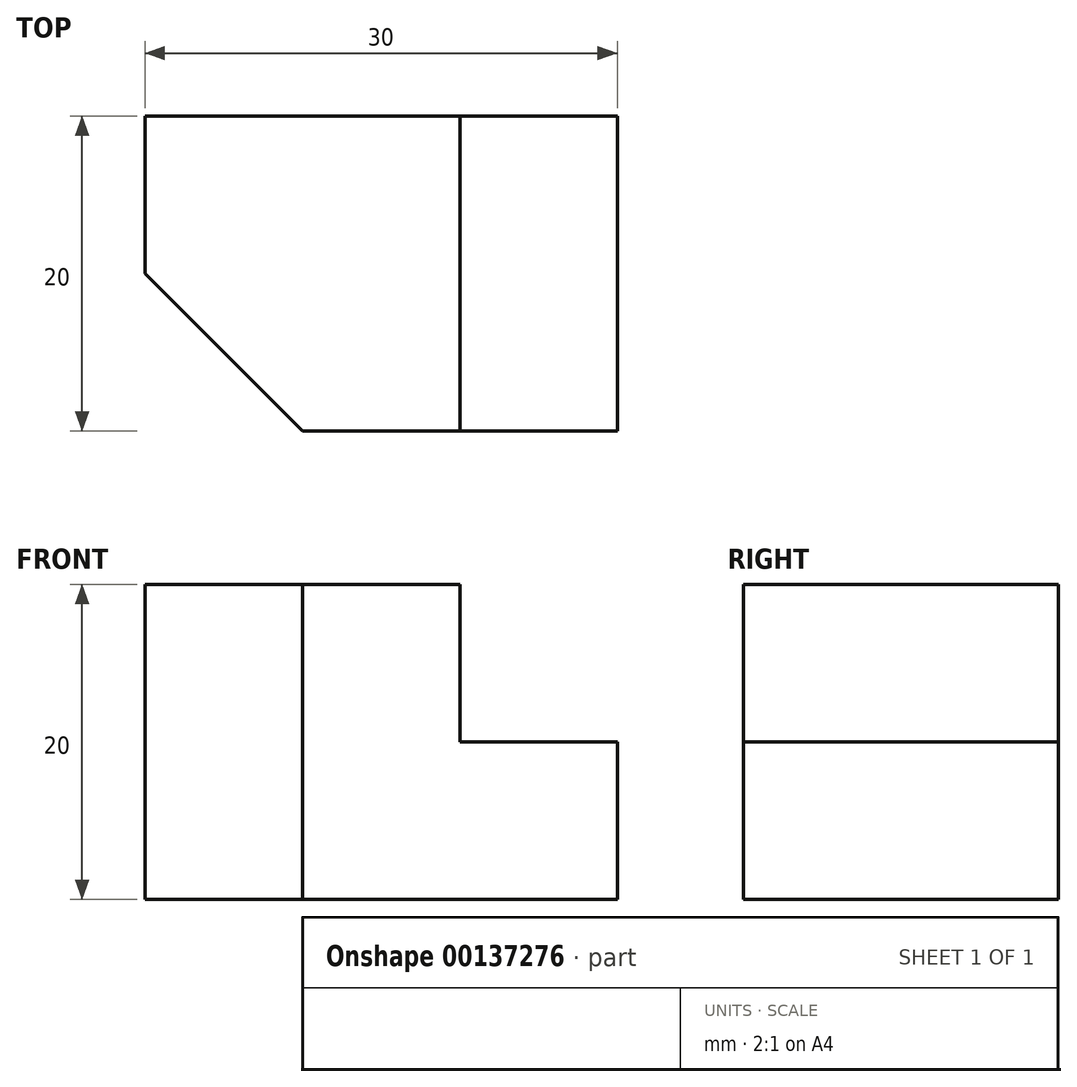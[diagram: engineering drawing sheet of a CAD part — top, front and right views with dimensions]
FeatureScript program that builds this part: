
annotation { "Feature Type Name" : "Feature", "Feature Type Description" : "" }
export const myFeature = defineFeature(function(context is Context, id is Id, definition is map)
    precondition{}
    {
        {
            var Q0;
            Q0=qCreatedBy(makeId("Front.planeOp"),FACE);
            var sketch = newSketch(context, id + "F0", { "sketchPlane" : qUnion([Q0])});
            skLineSegment(sketch, "E0", {"start": v(0, 0) * mm, "end": v(0, 20) * mm});
            skLineSegment(sketch, "E1", {"start": v(0, 20) * mm, "end": v(20, 20) * mm});
            skLineSegment(sketch, "E2", {"start": v(20, 20) * mm, "end": v(20, 10) * mm});
            skLineSegment(sketch, "E3", {"start": v(20, 10) * mm, "end": v(30, 10) * mm});
            skLineSegment(sketch, "E4", {"start": v(30, 10) * mm, "end": v(30, 0) * mm});
            skLineSegment(sketch, "E5", {"start": v(30, 0) * mm, "end": v(0, 0) * mm});
            skLineSegment(sketch, "E6", {"start": v(10, 0) * mm, "end": v(10, 20) * mm});
            skSolve(sketch);
        }
        {
            var Q0;
            {var subQ0=sQuery(id+"F0.wireOp",EDGE,"E0");Q0=makeQuery(id+"F0.imprint","IMPRINT",FACE,{"disambiguationData":[TD([[makeQuery(id+"F0.imprint","IMPRINT",EDGE,{"derivedFrom":subQ0}),-1.0]])]});}
            var Q1;
            {var subQ1=sQuery(id+"F0.wireOp",EDGE,"E2");Q1=makeQuery(id+"F0.imprint","IMPRINT",FACE,{"disambiguationData":[TD([[makeQuery(id+"F0.imprint","IMPRINT",EDGE,{"derivedFrom":subQ1}),-1.0]])]});}
            extrude(context, id + "F1", {"entities" : qUnion([Q0, Q1]), "depth" : 20 * mm});
        }
        {
            var Q0;
            Q0=makeQuery(id+"F1.opExtrude","SWEPT_FACE",FACE,{"disambiguationData":[OSD([sQuery(id+"F0.wireOp",EDGE,"E1")])]});
            var sketch = newSketch(context, id + "F2", { "sketchPlane" : qUnion([Q0])});
            skLineSegment(sketch, "E7", {"start": v(0, -10) * mm, "end": v(10, -20) * mm});
            skLineSegment(sketch, "E8", {"start": v(10, -20) * mm, "end": v(0, -20) * mm});
            skLineSegment(sketch, "E9", {"start": v(0, -20) * mm, "end": v(0, -10) * mm});
            skSolve(sketch);
        }
        {
            var Q0;
            Q0 = qSketchRegion(id + "F2", true);
            extrude(context, id + "F3", {"entities" : qUnion([Q0]), "operationType" : NewBodyOperationType.REMOVE, "endBound" : BoundingType.THROUGH_ALL, "oppositeDirection" : true, "depth" : 25 * mm});
        }
    });
